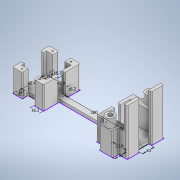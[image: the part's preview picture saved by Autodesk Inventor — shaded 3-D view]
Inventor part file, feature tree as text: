
AUTODESK INVENTOR PART (.ipt)
format: ipt  version: 2022 (Build 260153000, 153)  size: 341,504 bytes
history: native  units: mm
features: extrude x8, sketch x5, fillet x3, projected_geometry x2
ambient origin geometry x8: Origin, YZ Plane, XZ Plane, XY Plane, X Axis, Y Axis, Z Axis, Center Point
bodies: Solid1 (feature_tree)
feature tree (18):
  sketch  "Sketch1"  dims[d0=42.4mm d1=42.4mm]
  extrude  "Extrusion1"  Depth=42.4mm
  extrude  "Extrusion2"  Depth=5.0mm
  extrude  "Extrusion3"  Depth=16.2mm
  extrude  "Extrusion4"  Depth=16.2mm
  extrude  "Extrusion5"  Depth=15.0mm
  extrude  "Extrusion6"  Depth=100.0mm
  extrude  "Extrusion7"  Depth=5.0mm
  extrude  "Extrusion8"  Depth=10.0mm
  fillet  "Fillet1"  Radius=20.0mm
  fillet  "Fillet2"  Radius=22.8mm
  fillet  "Fillet3"  Radius=20.0mm
  sketch  "Sketch2"  dims[d2=10.0mm d3=5.0mm]
  sketch  "Sketch3"  dims[d4=16.2mm d5=16.2mm]
  sketch  "Sketch4"  dims[d6=16.2mm d7=16.2mm]
  projected_geometry  "Projected Loop1"
  sketch  "Sketch5"  dims[d8=15.0mm d9=15.0mm d12=100.0mm d13=5.0mm d14=10.0mm d16=20.0mm d17=22.8mm d18=20.0mm d19=5.0mm d20=0.0mm d21=38.8mm d22=0.0mm d23=38.8mm d24=0.0mm d25=78.8mm d26=0.0mm d27=4.3mm d28=1.25mm d29=2.5mm d30=5.0mm d31=0.0mm d32=7.5mm d33=8.1mm d34=15.0mm d35=0.0mm d36=2.5mm d37=5.0mm d38=0.0mm d39=2.5mm d40=5.0mm d41=0.0mm d42=2.0mm d43=2.0mm d44=2.0mm]
  projected_geometry  "Projected Loop2"
